# Revit family: WID
name_source: partatom
category: Generic Models
units: mm (PartAtom-declared; Revit-internal decimal feet)

## family parameters
Can host rebar = No
Cut with Voids When Loaded = No
Host = Face
Maintain Annotation Orientation = No
Part Type = Normal
Room Calculation Point = No
Round Connector Dimension = Use Diameter
Shared = No

## types (16) — shared parameters
Default Elevation = 4' - 0"
Description = EXTERIOR ACCESS DOOR / WALK-IN DOOR
Manufacturer = MIFAB
Material = <By Category>
Model = WID
URL = WWW.MIFAB.COM

## per-type parameters (varying)
| type | Height | Insulation Thickness | Width |
| WID-12"x24"x1" | 2' - 0" | 0' - 1" | 1' - 0" |
| WID-12"x12"x1" | 1' - 0" | 0' - 1" | 1' - 0" |
| WID-14"x14"x1" | 1' - 2" | 0' - 1" | 1' - 2" |
| WID-16"x16"x1" | 1' - 4" | 0' - 1" | 1' - 4" |
| WID-16"x20"x1" | 1' - 8" | 0' - 1" | 1' - 4" |
| WID-16"x36"x1" | 3' - 0" | 0' - 1" | 1' - 4" |
| WID-18"x18"x1" | 1' - 6" | 0' - 1" | 1' - 6" |
| WID-20"x30"x1" | 2' - 6" | 0' - 1" | 1' - 8" |
| WID-22"x30"x1" | 2' - 6" | 0' - 4" | 1' - 10" |
| WID-22"x36"x1" | 3' - 0" | 0' - 1" | 1' - 10" |
| WID-24"x24""x1" | 2' - 0" | 0' - 1" | 2' - 0" |
| WID-24"x36"x1" | 3' - 0" | 0' - 1" | 2' - 0" |
| WID-30"x30"x1" | 2' - 6" | 0' - 1" | 2' - 6" |
| WID-30'"x60"x1" | 5' - 0" | 0' - 1" | 2' - 6" |
| WID-36"x36"x1" | 3' - 0" | 0' - 1" | 3' - 0" |
| WID-36"x48"x1" | 4' - 0" | 0' - 1" | 3' - 0" |

## geometry (parser evidence)
native form markers: Sweep x6
no freeform markers — native parametric forms only
